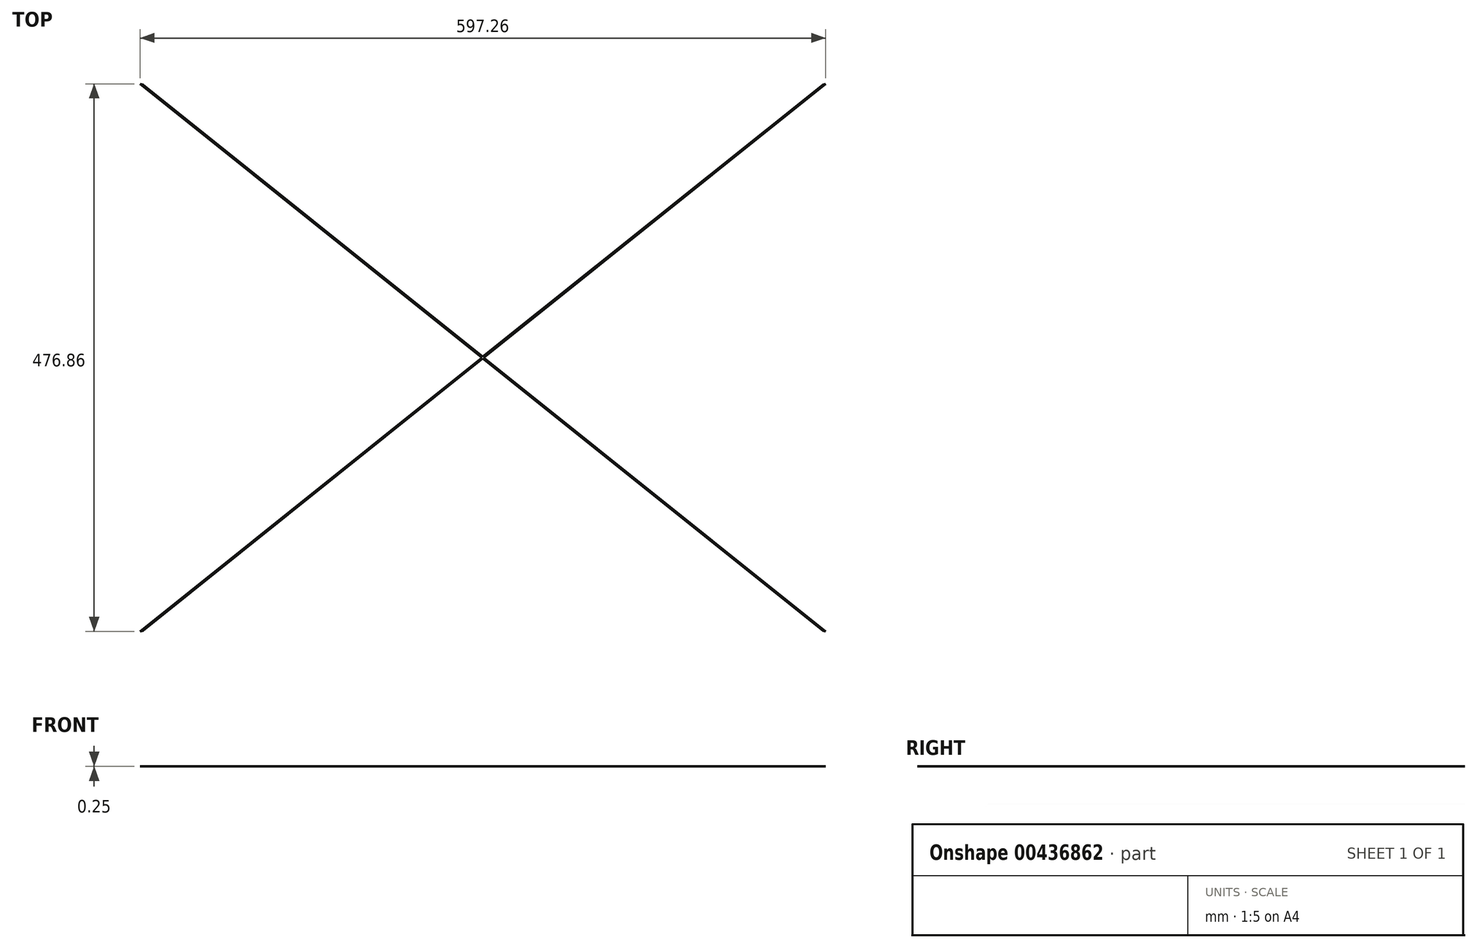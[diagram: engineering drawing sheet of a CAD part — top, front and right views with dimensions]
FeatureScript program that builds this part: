
annotation { "Feature Type Name" : "Feature", "Feature Type Description" : "" }
export const myFeature = defineFeature(function(context is Context, id is Id, definition is map)
    precondition{}
    {
        {
            var Q0;
            Q0=qCreatedBy(makeId("Top.planeOp"),FACE);
            var sketch = newSketch(context, id + "F0", { "sketchPlane" : qUnion([Q0])});
            skLineSegment(sketch, "E0", {"start": v(1.2, 0.32) * mm, "end": v(1.2, 0.32) * mm});
            skLineSegment(sketch, "E1", {"start": v(1.2, 0.32) * mm, "end": v(298.63, 238.43) * mm});
            skLineSegment(sketch, "E2", {"start": v(298.63, 238.43) * mm, "end": v(298.63, 238.43) * mm});
            skLineSegment(sketch, "E3", {"start": v(298.63, 238.43) * mm, "end": v(1.2, 0.32) * mm});
            skLineSegment(sketch, "E4", {"start": v(-1.2, -0.32) * mm, "end": v(296.22, 237.8) * mm});
            skLineSegment(sketch, "E5", {"start": v(298.63, 238.43) * mm, "end": v(296.22, 237.8) * mm});
            skLineSegment(sketch, "E6.MirrorCS", {"start": v(298.63, -238.43) * mm, "end": v(296.22, -237.8) * mm});
            skLineSegment(sketch, "E7.MirrorCS", {"start": v(1.2, -0.32) * mm, "end": v(298.63, -238.43) * mm});
            skLineSegment(sketch, "E8.MirrorCS", {"start": v(1.2, -0.32) * mm, "end": v(1.2, -0.32) * mm});
            skLineSegment(sketch, "E9.MirrorCS", {"start": v(298.63, -238.43) * mm, "end": v(1.2, -0.32) * mm});
            skLineSegment(sketch, "E10.MirrorCS", {"start": v(298.63, -238.43) * mm, "end": v(298.63, -238.43) * mm});
            skLineSegment(sketch, "E11.MirrorCS", {"start": v(-1.2, 0.32) * mm, "end": v(296.22, -237.8) * mm});
            skLineSegment(sketch, "E12.MirrorCS", {"start": v(-298.63, -238.43) * mm, "end": v(-296.22, -237.8) * mm});
            skLineSegment(sketch, "E13.MirrorCS", {"start": v(-298.63, 238.43) * mm, "end": v(-296.22, 237.8) * mm});
            skLineSegment(sketch, "E14.MirrorCS", {"start": v(-1.2, 0.32) * mm, "end": v(-298.63, 238.43) * mm});
            skLineSegment(sketch, "E15.MirrorCS", {"start": v(-1.2, -0.32) * mm, "end": v(-298.63, -238.43) * mm});
            skLineSegment(sketch, "E16.MirrorCS", {"start": v(1.2, 0.32) * mm, "end": v(-296.22, -237.8) * mm});
            skLineSegment(sketch, "E17.MirrorCS", {"start": v(-298.63, 238.43) * mm, "end": v(-298.63, 238.43) * mm});
            skLineSegment(sketch, "E18.MirrorCS", {"start": v(-1.2, -0.32) * mm, "end": v(-1.2, -0.32) * mm});
            skLineSegment(sketch, "E19.MirrorCS", {"start": v(-298.63, -238.43) * mm, "end": v(-298.63, -238.43) * mm});
            skLineSegment(sketch, "E20.MirrorCS", {"start": v(-1.2, 0.32) * mm, "end": v(-1.2, 0.32) * mm});
            skLineSegment(sketch, "E21.MirrorCS", {"start": v(-298.63, -238.43) * mm, "end": v(-1.2, -0.32) * mm});
            skLineSegment(sketch, "E22.MirrorCS", {"start": v(-298.63, 238.43) * mm, "end": v(-1.2, 0.32) * mm});
            skLineSegment(sketch, "E23.MirrorCS", {"start": v(1.2, -0.32) * mm, "end": v(-296.22, 237.8) * mm});
            skSolve(sketch);
        }
        {
            var Q0;
            Q0 = qSketchRegion(id + "F0", true);
            extrude(context, id + "F1", {"entities" : qUnion([Q0]), "depth" : 0.25 * mm});
        }
    });
